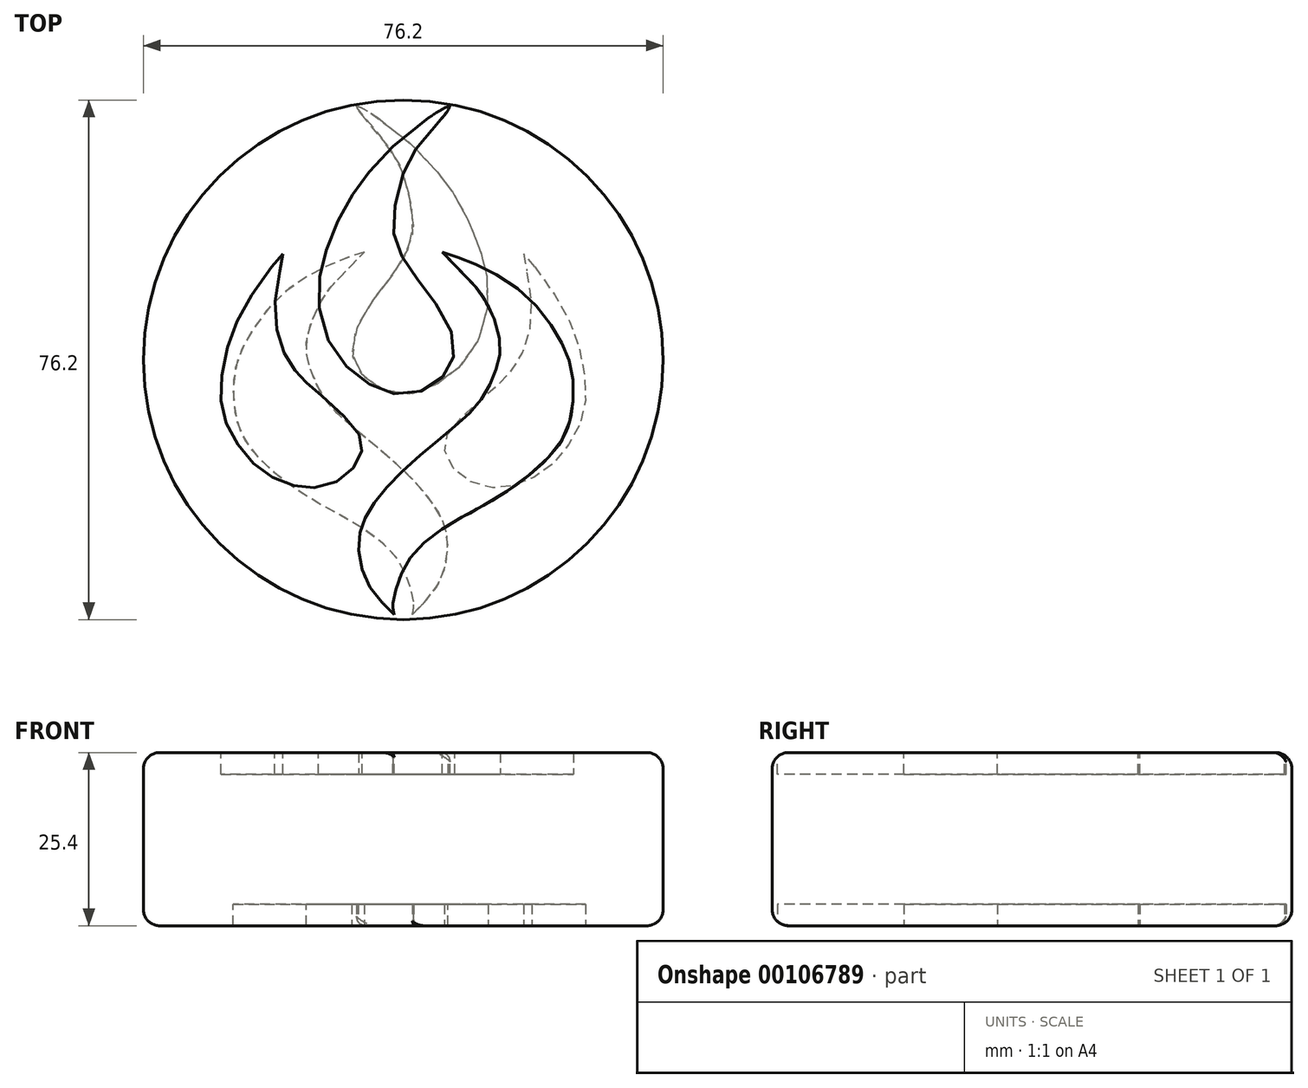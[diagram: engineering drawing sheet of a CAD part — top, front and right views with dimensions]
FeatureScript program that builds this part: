
annotation { "Feature Type Name" : "Feature", "Feature Type Description" : "" }
export const myFeature = defineFeature(function(context is Context, id is Id, definition is map)
    precondition{}
    {
        {
            var Q0;
            Q0=qCreatedBy(makeId("Top.planeOp"),FACE);
            var sketch = newSketch(context, id + "F0", { "sketchPlane" : qUnion([Q0])});
            skCircle(sketch, "E0", {"center": v(0, 0) * mm, "radius": 38.1 * mm});
            skSolve(sketch);
        }
        {
            var Q0;
            Q0 = qSketchRegion(id + "F0", true);
            extrude(context, id + "F1", {"entities" : qUnion([Q0]), "depth" : 12.7 * mm});
        }
        {
            var Q0;
            Q0=makeQuery(id+"F1.opExtrude","CAP_FACE",FACE,{"disambiguationData":[OSD([sQuery(id+"F0.wireOp",EDGE,"E0")])],"isStart":false});
            var sketch = newSketch(context, id + "F2", { "sketchPlane" : qUnion([Q0])});
            skFitSpline(sketch, "E1", {"points": [v(6.74, 37.08) * mm, v(0, 32.64) * mm, v(-5.67, 26.66) * mm, v(-8.52, 22.46) * mm, v(-11.13, 16.46) * mm, v(-12.31, 11.8) * mm, v(-11.84, 5.08) * mm, v(-8.46, -0.84) * mm, v(-4.19, -3.97) * mm, v(0, -5.08) * mm, v(4.58, -3.62) * mm, v(6.9, -0.82) * mm, v(7.47, 2.54) * mm, v(4.87, 8.14) * mm, v(1.32, 12.74) * mm, v(-0.94, 16.72) * mm, v(-1.5, 20.6) * mm, v(0, 27.29) * mm, v(2.6, 31.85) * mm, v(6.74, 37.08) * mm]});
            skFitSpline(sketch, "E2", {"points": [v(-22.08, 9.73) * mm, v(-25.38, 3.17) * mm, v(-26.7, -3.43) * mm, v(-26.33, -8.27) * mm, v(-24.16, -12.63) * mm, v(-20.73, -16.25) * mm, v(-16.68, -18.28) * mm, v(-12.99, -18.78) * mm, v(-8.77, -17.28) * mm, v(-6.5, -14.52) * mm, v(-6.07, -12.04) * mm, v(-7.8, -9.23) * mm, v(-12.91, -4.5) * mm, v(-14.77, -2.84) * mm, v(-16.53, -0.7) * mm, v(-18.31, 3.27) * mm, v(-18.66, 10.12) * mm, v(-18.12, 14.58) * mm, v(-22.08, 9.73) * mm]});
            skLineSegment(sketch, "E3", {"start": v(-19.28, 13.62) * mm, "end": v(-17.65, 15.56) * mm});
            skLineSegment(sketch, "E4", {"start": v(-17.65, 15.56) * mm, "end": v(-18.13, 13.04) * mm});
            skLineSegment(sketch, "E5", {"start": v(4.76, 36.17) * mm, "end": v(6.85, 37.26) * mm});
            skLineSegment(sketch, "E6", {"start": v(6.85, 37.26) * mm, "end": v(6.64, 36.73) * mm});
            skFitSpline(sketch, "E7", {"points": [v(5.74, 15.79) * mm, v(9.83, 14.33) * mm, v(17.2, 10.07) * mm, v(22.58, 3.63) * mm, v(24.66, -1.45) * mm, v(24.64, -8.03) * mm, v(22.1, -13.4) * mm, v(14.03, -20.04) * mm, v(6.17, -24.53) * mm, v(1.06, -28.96) * mm, v(-0.9, -33.07) * mm, v(-1.53, -35.98) * mm, v(-1.32, -37.37) * mm], "startDerivative": vector(52.68, -16.83) * mm, "endDerivative": vector(8.02, -31.27) * mm});
            skFitSpline(sketch, "E8", {"points": [v(-1.32, -37.37) * mm, v(-5.48, -32.24) * mm, v(-6.48, -26.18) * mm, v(-4.9, -21.92) * mm, v(0, -16.22) * mm, v(7.06, -10.2) * mm, v(11.46, -5.77) * mm, v(13.6, -1.4) * mm, v(14.18, 2.75) * mm, v(11.72, 9.17) * mm, v(8.93, 12.48) * mm, v(5.74, 15.79) * mm], "startDerivative": vector(-49.87, 48.78) * mm, "endDerivative": vector(-40.46, 42.35) * mm});
            skSolve(sketch);
        }
        {
            var Q0;
            Q0 = qSketchRegion(id + "F2", true);
            extrude(context, id + "F3", {"entities" : qUnion([Q0]), "operationType" : NewBodyOperationType.REMOVE, "oppositeDirection" : true, "depth" : 3.17 * mm});
        }
        {
            var Q0;
            Q0=qCreatedBy(makeId("Right.planeOp"),FACE);
            var sketch = newSketch(context, id + "F4", { "sketchPlane" : qUnion([Q0])});
            skLineSegment(sketch, "E9", {"start": v(46.4, 0) * mm, "end": v(-41.67, 0) * mm, "construction": true});
            skSolve(sketch);
        }
        {
            var Q0;
            Q0=makeQuery(id+"F1.opExtrude","SWEPT_BODY",BODY,{"disambiguationData":[OSD([sQuery(id+"F0.wireOp",EDGE,"E0")])]});
            var Q1;
            Q1=sQuery(id+"F4.wireOp",EDGE,"E9");
            circularPattern(context, id + "F5", {"entities" : qUnion([Q0]), "axis" : qUnion([Q1]), "angle" : 180 * degree, "instanceCount" : 2});
        }
        {
            var Q0;
            Q0=makeQuery(id+"F5.opPattern","COPY",EDGE,{"derivedFrom":makeQuery(id+"F1.opExtrude","CAP_EDGE",EDGE,{"disambiguationData":[OSD([sQuery(id+"F0.wireOp",EDGE,"E0")])],"isStart":false}),"instanceName":"1"});
            var Q1;
            Q1=makeQuery(id+"F1.opExtrude","CAP_EDGE",EDGE,{"disambiguationData":[OSD([sQuery(id+"F0.wireOp",EDGE,"E0")])],"isStart":false});
            fillet(context, id + "F6", {"entities" : qUnion([Q0, Q1]), "radius" : 2.38 * mm, "tangentPropagation" : true, "allowEdgeOverflow" : false});
        }
        {
            var Q0;
            Q0=makeQuery(id+"F5.opPattern","COPY",FACE,{"derivedFrom":makeQuery(id+"F1.opExtrude","CAP_FACE",FACE,{"disambiguationData":[OSD([sQuery(id+"F0.wireOp",EDGE,"E0")])],"isStart":true}),"instanceName":"1"});
            extrude(context, id + "F7", {"entities" : qUnion([Q0]), "operationType" : NewBodyOperationType.ADD, "depth" : 3.17 * mm});
        }
    });
